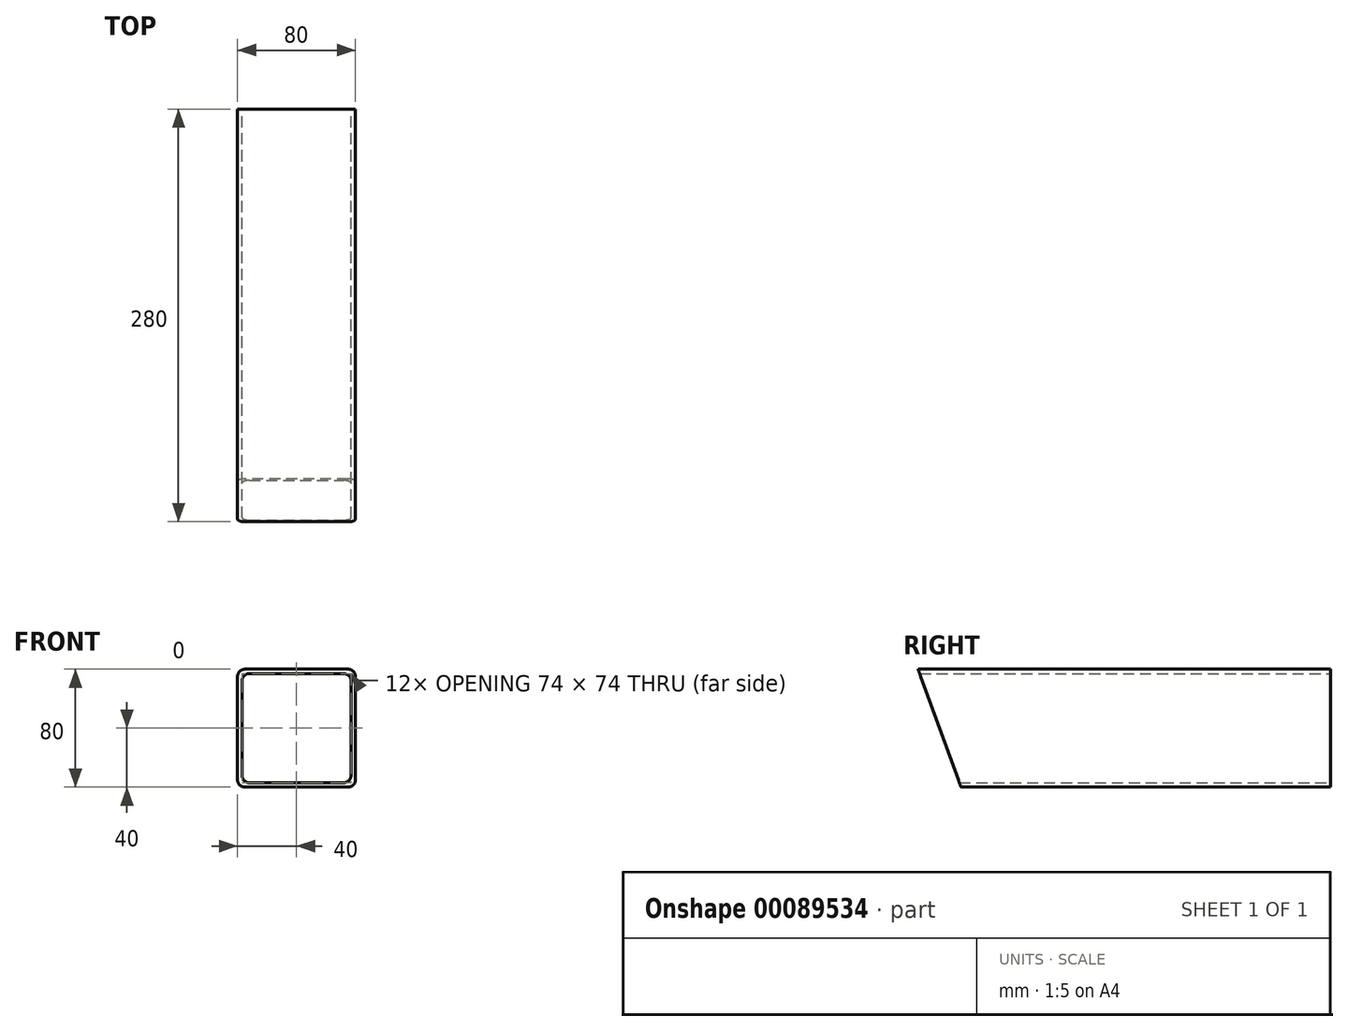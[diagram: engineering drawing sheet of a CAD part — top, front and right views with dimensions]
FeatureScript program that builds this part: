
annotation { "Feature Type Name" : "Feature", "Feature Type Description" : "" }
export const myFeature = defineFeature(function(context is Context, id is Id, definition is map)
    precondition{}
    {
        {
            var Q0;
            Q0=qCreatedBy(makeId("Front.planeOp"),FACE);
            var sketch = newSketch(context, id + "F0", { "sketchPlane" : qUnion([Q0])});
            skLineSegment(sketch, "E0.bottom", {"start": v(40, -40) * mm, "end": v(-40, -40) * mm});
            skLineSegment(sketch, "E0.top", {"start": v(40, 40) * mm, "end": v(-40, 40) * mm});
            skLineSegment(sketch, "E0.left", {"start": v(40, -40) * mm, "end": v(40, 40) * mm});
            skLineSegment(sketch, "E0.right", {"start": v(-40, -40) * mm, "end": v(-40, 40) * mm});
            skPoint(sketch, "E0.middle", {"position": v(0, 0) * mm});
            skLineSegment(sketch, "E1.0", {"start": v(37, 37) * mm, "end": v(-37, 37) * mm});
            skLineSegment(sketch, "E1.1", {"start": v(37, -37) * mm, "end": v(37, 37) * mm});
            skLineSegment(sketch, "E1.2", {"start": v(37, -37) * mm, "end": v(-37, -37) * mm});
            skLineSegment(sketch, "E1.3", {"start": v(-37, -37) * mm, "end": v(-37, 37) * mm});
            skSolve(sketch);
        }
        {
            var Q0;
            Q0=makeQuery(id+"F0.imprint","IMPRINT",FACE,{"disambiguationData":[TD([[makeQuery(id+"F0.imprint","IMPRINT",EDGE,{"derivedFrom":sQuery(id+"F0.wireOp",EDGE,"E0.bottom")}),-1.0]])]});
            extrude(context, id + "F1", {"entities" : qUnion([Q0]), "depth" : 280 * mm});
        }
        {
            var Q0;
            Q0=makeQuery(id+"F1.opExtrude","SWEPT_FACE",FACE,{"disambiguationData":[OSD([sQuery(id+"F0.wireOp",EDGE,"E0.right")])]});
            var sketch = newSketch(context, id + "F2", { "sketchPlane" : qUnion([Q0])});
            skLineSegment(sketch, "E2", {"start": v(280, 40) * mm, "end": v(250.88, -40) * mm});
            skSolve(sketch);
        }
        {
            var Q0;
            {var subQ0=sQuery(id+"F2.wireOp",EDGE,"E2");Q0=makeQuery(id+"F2.imprint","IMPRINT",FACE,{"disambiguationData":[TD([[makeQuery(id+"F2.imprint","IMPRINT",EDGE,{"derivedFrom":subQ0}),1.0]])]});}
            extrude(context, id + "F3", {"entities" : qUnion([Q0]), "operationType" : NewBodyOperationType.REMOVE, "endBound" : BoundingType.THROUGH_ALL, "oppositeDirection" : true, "depth" : 25 * mm});
        }
        {
            var Q0;
            Q0=makeQuery(id+"F1.opExtrude","SWEPT_FACE",FACE,{"disambiguationData":[OSD([sQuery(id+"F0.wireOp",EDGE,"E0.bottom")])]});
            var sketch = newSketch(context, id + "F4", { "sketchPlane" : qUnion([Q0])});
            skLineSegment(sketch, "E3", {"start": v(0, 0) * mm, "end": v(0, 250.88) * mm, "construction": true});
            skLineSegment(sketch, "E4", {"start": v(-40, 50) * mm, "end": v(40, 50) * mm, "construction": true});
            skLineSegment(sketch, "E5.0", {"start": v(-37, 251.97) * mm, "end": v(37, 251.97) * mm});
            skArc(sketch, "E6", {"start": v(5, 251.97) * mm, "mid": v(0, 246.97) * mm, "end": v(-5, 251.97) * mm});
            skSolve(sketch);
        }
        {
            var Q0;
            Q0=makeQuery(id+"F4.imprint","IMPRINT",FACE,{"disambiguationData":[TD([[makeQuery(id+"F4.imprint","IMPRINT",EDGE,{"derivedFrom":sQuery(id+"F4.wireOp",EDGE,"F2YR0NjR-wKQj-UdcN-LWiY-nTZFwQylV7Vi")}),1.0]])]});
            var Q1;
            {var subQ0=sQuery(id+"F4.wireOp",EDGE,"E6");var subQ1=makeQuery(id+"F3.boolean.opBoolean","COPY",EDGE,{"derivedFrom":makeQuery(id+"F3.opExtrude","SWEPT_EDGE",EDGE,{"disambiguationData":[OSD([sQuery(id+"F0.wireOp",EDGE,"E0.bottom"),sQuery(id+"F0.wireOp",EDGE,"E0.right"),sQuery(id+"F2.wireOp",EDGE,"E2")])]})});var subQ2=makeQuery(id+"F4.imprint","INTERSECT",VERTEX,{"disambiguationData":[OD(0.0)],"derivedFrom":[subQ1,subQ0]});Q1=makeQuery(id+"F4.imprint","IMPRINT",FACE,{"disambiguationData":[TD([[makeQuery(id+"F4.imprint","IMPRINT",EDGE,{"disambiguationData":[TD([[subQ2,-1.0]])],"derivedFrom":subQ0}),-1.0]])]});}
            var Q2;
            {var subQ0=sQuery(id+"F4.wireOp",EDGE,"E6");var subQ1=sQuery(id+"F4.wireOp",EDGE,"E5.0");var subQ2=makeQuery(id+"F4.imprint","INTERSECT",VERTEX,{"disambiguationData":[OD(0.0)],"derivedFrom":[subQ1,subQ0]});Q2=makeQuery(id+"F4.imprint","IMPRINT",FACE,{"disambiguationData":[TD([[makeQuery(id+"F4.imprint","IMPRINT",EDGE,{"disambiguationData":[TD([[subQ2,1.0]])],"derivedFrom":subQ1}),-1.0]])]});}
            extrude(context, id + "F5", {"entities" : qUnion([Q0, Q1, Q2]), "operationType" : NewBodyOperationType.REMOVE, "endBound" : BoundingType.UP_TO_NEXT, "oppositeDirection" : true, "depth" : 25 * mm});
        }
        {
            var Q0;
            Q0=makeQuery(id+"F1.opExtrude","SWEPT_EDGE",EDGE,{"disambiguationData":[OSD([sQuery(id+"F0.wireOp",EDGE,"E0.top"),sQuery(id+"F0.wireOp",EDGE,"E0.left")])]});
            var Q1;
            Q1=makeQuery(id+"F1.opExtrude","SWEPT_EDGE",EDGE,{"disambiguationData":[OSD([sQuery(id+"F0.wireOp",EDGE,"E0.bottom"),sQuery(id+"F0.wireOp",EDGE,"E0.left")])]});
            var Q2;
            Q2=makeQuery(id+"F1.opExtrude","SWEPT_EDGE",EDGE,{"disambiguationData":[OSD([sQuery(id+"F0.wireOp",EDGE,"E0.top"),sQuery(id+"F0.wireOp",EDGE,"E0.right")])]});
            var Q3;
            Q3=makeQuery(id+"F1.opExtrude","SWEPT_EDGE",EDGE,{"disambiguationData":[OSD([sQuery(id+"F0.wireOp",EDGE,"E0.bottom"),sQuery(id+"F0.wireOp",EDGE,"E0.right")])]});
            var Q4;
            Q4=makeQuery(id+"F1.opExtrude","SWEPT_EDGE",EDGE,{"disambiguationData":[OSD([sQuery(id+"F0.wireOp",EDGE,"E1.0"),sQuery(id+"F0.wireOp",EDGE,"E1.1")])]});
            var Q5;
            Q5=makeQuery(id+"F1.opExtrude","SWEPT_EDGE",EDGE,{"disambiguationData":[OSD([sQuery(id+"F0.wireOp",EDGE,"E1.1"),sQuery(id+"F0.wireOp",EDGE,"E1.2")])]});
            var Q6;
            Q6=makeQuery(id+"F1.opExtrude","SWEPT_EDGE",EDGE,{"disambiguationData":[OSD([sQuery(id+"F0.wireOp",EDGE,"E1.2"),sQuery(id+"F0.wireOp",EDGE,"E1.3")])]});
            var Q7;
            Q7=makeQuery(id+"F1.opExtrude","SWEPT_EDGE",EDGE,{"disambiguationData":[OSD([sQuery(id+"F0.wireOp",EDGE,"E1.0"),sQuery(id+"F0.wireOp",EDGE,"E1.3")])]});
            fillet(context, id + "F6", {"entities" : qUnion([Q0, Q1, Q2, Q3, Q4, Q5, Q6, Q7]), "radius" : 5 * mm, "tangentPropagation" : true, "allowEdgeOverflow" : false});
        }
    });
